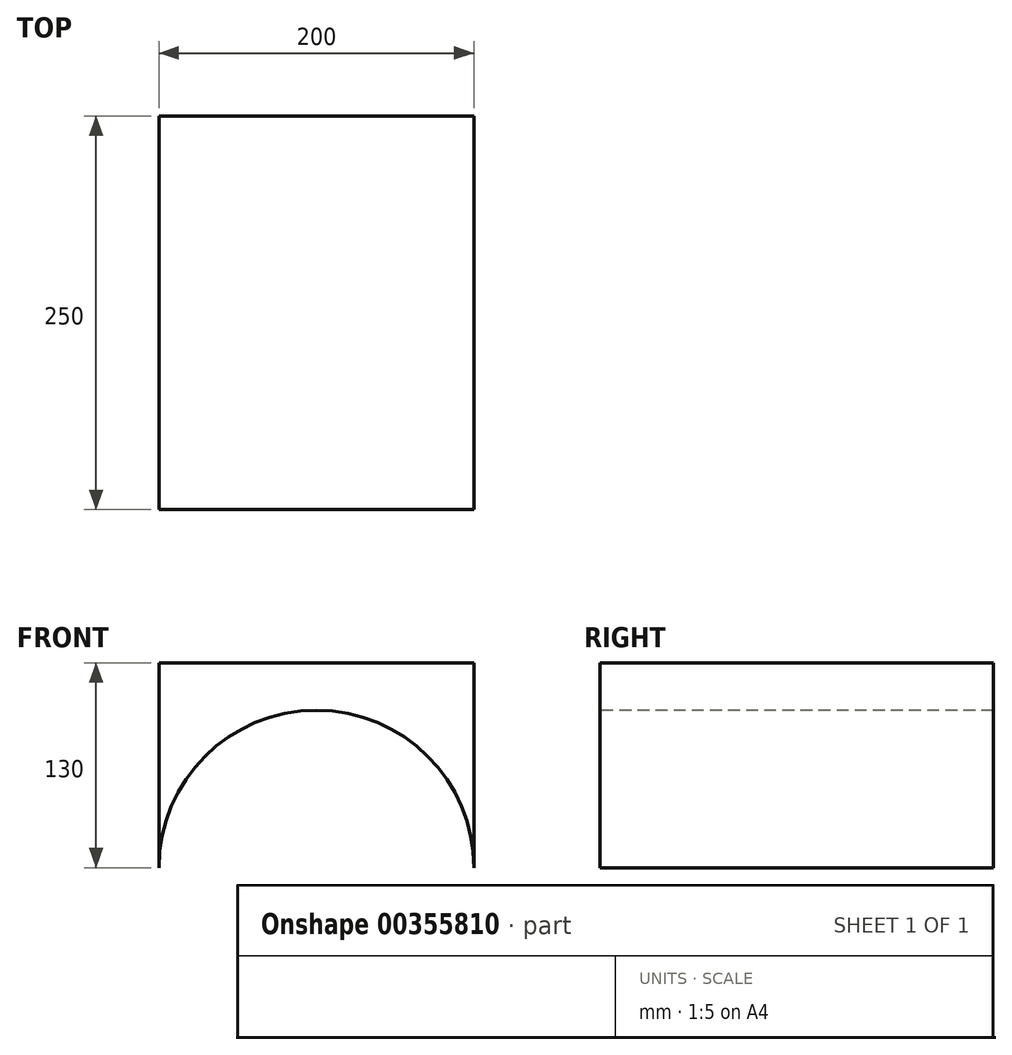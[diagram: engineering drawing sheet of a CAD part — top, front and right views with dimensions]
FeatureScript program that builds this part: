
annotation { "Feature Type Name" : "Feature", "Feature Type Description" : "" }
export const myFeature = defineFeature(function(context is Context, id is Id, definition is map)
    precondition{}
    {
        {
            var Q0;
            Q0=qCreatedBy(makeId("Front.planeOp"),FACE);
            var sketch = newSketch(context, id + "F0", { "sketchPlane" : qUnion([Q0])});
            skArc(sketch, "E0", {"start": v(100, 0) * mm, "mid": v(0, 100) * mm, "end": v(-100, 0) * mm});
            skLineSegment(sketch, "E1", {"start": v(-100, 0) * mm, "end": v(-100, 130) * mm});
            skLineSegment(sketch, "E2", {"start": v(-100, 130) * mm, "end": v(100, 130) * mm});
            skLineSegment(sketch, "E3", {"start": v(100, 130) * mm, "end": v(100, 0) * mm});
            skSolve(sketch);
        }
        {
            var Q0;
            Q0=qSketchRegion(id+"F0",true);
            extrude(context, id + "F1", {"entities" : qUnion([Q0]), "oppositeDirection" : true, "depth" : 250 * mm});
        }
    });
